# Revit family: Operable-Walls_Modernfold_Legacy-Premier_Paired-Panels_Expandable-Panel
name_source: partatom
category: Specialty Equipment
units: mm (PartAtom-declared; Revit-internal decimal feet)

## family parameters
Always vertical = Yes
Classification Number = 23.25.40.17.14
Cut with Voids When Loaded = No
Enable Cutting in Views = No
Maintain Annotation Orientation = No
Part Type = Normal
Room Calculation Point = No
Round Connector Dimension = Use Diameter
Shared = No
Work Plane-Based = No

## types (2) — shared parameters
Bottom Seal Height = 0' - 2"
Default Elevation = 0' - 0"
Manufacturer = Modernfold
Model = Acousti-Seal® Legacy® & Premier®
Panel Material = Wall Finish - Modernfold - Grey
Panel Thickness = 0' - 3"
Seal Width = 0' - 1 1/2"
Track Material = Track Color - Modernfold - White
Track Trim = 0' - 1"
Trim Material = Trim Color - Modernfold-Sherwin Williams® - Natural Choice
URL = https://www.modernfold.com

## per-type parameters (varying)
| type | Description | zNoPckt | zTypIII |
| No Pocket Door | Legacy/Premier - Expandable Panel - Paired Panels - No Pocket Door | Yes | No |
| Pocket Door Type III | Legacy/Premier - Expandable Panel - Paired Panels - Pocket Door Type III | No | Yes |

## geometry (parser evidence)
native form markers: Sweep x24
no freeform markers — native parametric forms only
